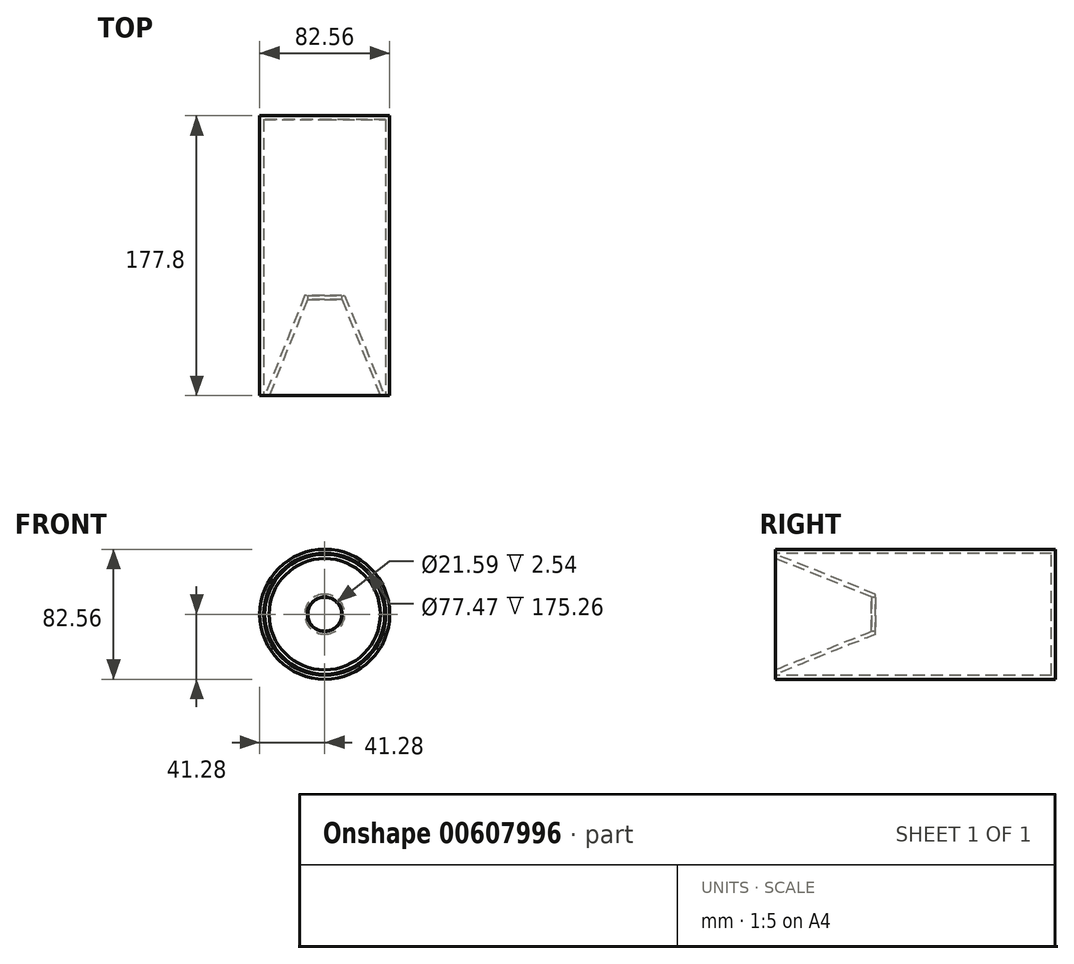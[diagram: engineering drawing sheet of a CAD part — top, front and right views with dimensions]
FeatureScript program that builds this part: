
annotation { "Feature Type Name" : "Feature", "Feature Type Description" : "" }
export const myFeature = defineFeature(function(context is Context, id is Id, definition is map)
    precondition{}
    {
        {
            var Q0;
            Q0=qCreatedBy(makeId("Front.planeOp"),FACE);
            var sketch = newSketch(context, id + "F0", { "sketchPlane" : qUnion([Q0])});
            skCircle(sketch, "E0", {"center": v(0, 0) * mm, "radius": 38.1 * mm});
            skSolve(sketch);
        }
        {
            var Q0;
            Q0=qCreatedBy(makeId("Front.planeOp"),FACE);
            var sketch = newSketch(context, id + "F1", { "sketchPlane" : qUnion([Q0])});
            skCircle(sketch, "E1", {"center": v(58.29, 58) * mm, "radius": 3.18 * mm});
            skSolve(sketch);
        }
        {
            var Q0;
            Q0 = qSketchRegion(id + "F1", true);
            extrude(context, id + "F2", {"entities" : qUnion([Q0]), "oppositeDirection" : true, "depth" : 63.5 * mm, "offsetDistance" : 25.4 * mm});
        }
        {
            var Q0;
            Q0=makeQuery(id+"F2.opExtrude","CAP_FACE",FACE,{"disambiguationData":[OSD([sQuery(id+"F1.wireOp",EDGE,"E1")])],"isStart":false});
            var sketch = newSketch(context, id + "F3", { "sketchPlane" : qUnion([Q0])});
            skCircle(sketch, "E2", {"center": v(0, 0) * mm, "radius": 12.7 * mm});
            skSolve(sketch);
        }
        {
            var Q0;
            Q0=makeQuery(id+"F0.imprint","IMPRINT",FACE,{"disambiguationData":[TD([[makeQuery(id+"F0.imprint","IMPRINT",EDGE,{"derivedFrom":sQuery(id+"F0.wireOp",EDGE,"E0")}),1.0]])]});
            var Q1;
            Q1=makeQuery(id+"F3.imprint","IMPRINT",FACE,{"disambiguationData":[TD([[makeQuery(id+"F3.imprint","IMPRINT",EDGE,{"derivedFrom":sQuery(id+"F3.wireOp",EDGE,"E2")}),1.0]])]});
            loft(context, id + "F4", {"sheetProfilesArray" : [{ "sheetProfileEntities" : qUnion([Q0]) }, { "sheetProfileEntities" : qUnion([Q1]) }]});
        }
        {
            var Q0;
            Q0=makeQuery(id+"F4.opLoft","CAP_FACE",FACE,{"disambiguationData":[OSD([makeQuery(id+"F0.imprint","IMPRINT",FACE,{"disambiguationData":[TD([[makeQuery(id+"F0.imprint","IMPRINT",EDGE,{"derivedFrom":sQuery(id+"F0.wireOp",EDGE,"E0")}),1.0]])]})])],"isStart":true});
            shell(context, id + "F5", {"entities" : qUnion([Q0]), "thickness" : 2.54 * mm});
        }
        {
            var Q0;
            Q0=qCreatedBy(makeId("Front.planeOp"),FACE);
            var sketch = newSketch(context, id + "F6", { "sketchPlane" : qUnion([Q0])});
            skCircle(sketch, "E3", {"center": v(0, 0) * mm, "radius": 10.8 * mm});
            skSolve(sketch);
        }
        {
            var Q0;
            Q0 = qSketchRegion(id + "F6", true);
            extrude(context, id + "F7", {"entities" : qUnion([Q0]), "operationType" : NewBodyOperationType.REMOVE, "oppositeDirection" : true, "depth" : 136.4 * mm, "offsetDistance" : 25.4 * mm});
        }
        {
            var Q0;
            Q0=makeQuery(id+"F2.opExtrude","SWEPT_BODY",BODY,{"disambiguationData":[OSD([sQuery(id+"F1.wireOp",EDGE,"E1")])]});
            deleteBodies(context, id + "F8", {"entities" : qUnion([Q0])});
        }
        {
            var Q0;
            Q0=qCreatedBy(makeId("Front.planeOp"),FACE);
            var sketch = newSketch(context, id + "F9", { "sketchPlane" : qUnion([Q0])});
            skCircle(sketch, "E4", {"center": v(0, 0) * mm, "radius": 41.28 * mm});
            skSolve(sketch);
        }
        {
            var Q0;
            Q0=makeQuery(id+"F9.imprint","IMPRINT",FACE,{"disambiguationData":[TD([[makeQuery(id+"F9.imprint","IMPRINT",EDGE,{"derivedFrom":sQuery(id+"F9.wireOp",EDGE,"E4")}),1.0]])]});
            extrude(context, id + "F10", {"entities" : qUnion([Q0]), "oppositeDirection" : true, "depth" : 177.8 * mm, "offsetDistance" : 25.4 * mm});
        }
        {
            var Q0;
            Q0=makeQuery(id+"F10.opExtrude","CAP_FACE",FACE,{"disambiguationData":[OSD([sQuery(id+"F9.wireOp",EDGE,"E4")])],"isStart":true});
            shell(context, id + "F11", {"entities" : qUnion([Q0]), "thickness" : 2.54 * mm});
        }
    });
